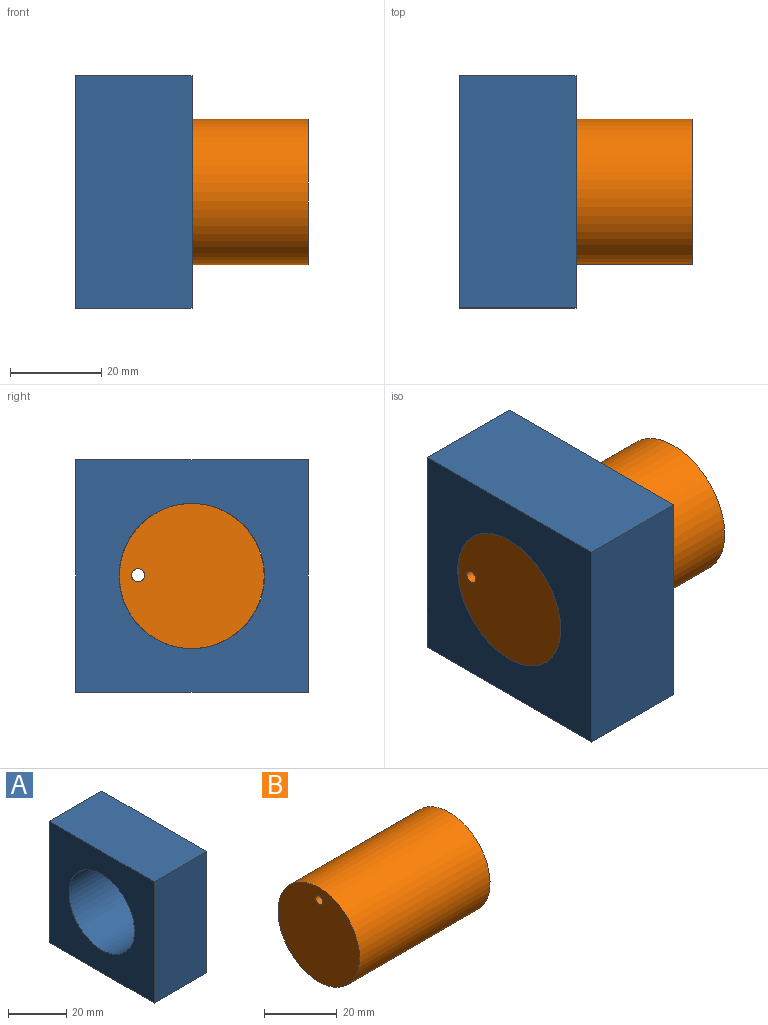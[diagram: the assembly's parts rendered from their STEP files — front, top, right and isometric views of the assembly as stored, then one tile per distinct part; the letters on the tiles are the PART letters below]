
ASSEMBLY  parts=2 mates=1
PART A: 7 faces, bbox 25.4x50.8x50.8 mm
  f0: plane 50.8x25.4mm, normal (0,0,-1), area 1290.3mm2, adj f1,f4,f5,f6
  f1: plane 50.8x25.4mm, normal (0,1,0), area 1290.3mm2, adj f0,f2,f5,f6
  f2: plane 50.8x25.4mm, normal (0,0,1), area 1290.3mm2, adj f1,f4,f5,f6
  f3: cylinder r=15.88mm len=31.75mm, axis (-1,0,0), area 2533.5mm2, adj f5,f6
  f4: plane 50.8x25.4mm, normal (0,-1,0), area 1290.3mm2, adj f0,f2,f5,f6
  f5: plane 50.8x50.8mm, normal (1,0,0), area 1788.9mm2, adj f0,f1,f2,f3,f4
  f6: plane 50.8x50.8mm, normal (-1,0,0), area 1788.9mm2, adj f0,f1,f2,f3,f4
PART B: 4 faces, bbox 50.8x31.8x31.8 mm
  f0: cylinder r=1.43mm len=50.8mm, axis (-1,0,0), area 456.1mm2, adj f2,f3
  f1: cylinder r=15.88mm len=50.8mm, axis (-1,0,0), area 5067.1mm2, adj f2,f3
  f2: plane 31.75x31.75mm, normal (1,0,0), area 785.3mm2, adj f0,f1
  f3: plane 31.75x31.75mm, normal (-1,0,0), area 785.3mm2, adj f0,f1
PLACE A at identity fixed
PLACE B rot(axis=(-1,0,0),90deg) t=(0,25.48,-18.64)mm
MATE ball B.f3 <-> A.f3  axis (-1,0,0) through (0,47.23,-52.86)mm
